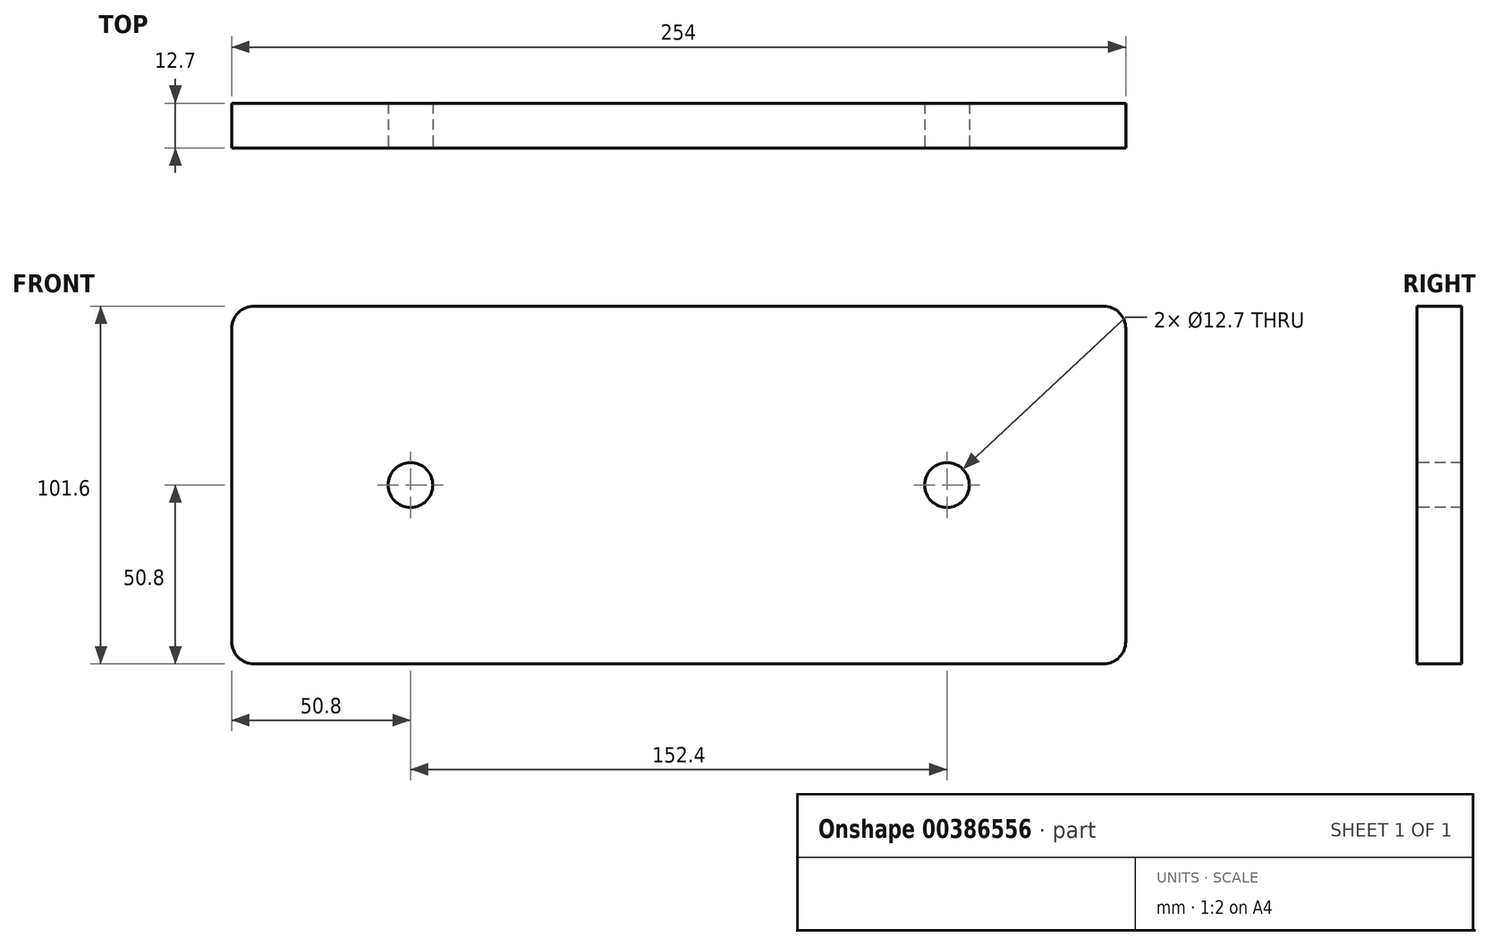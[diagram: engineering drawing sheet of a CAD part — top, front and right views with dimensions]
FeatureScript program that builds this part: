
annotation { "Feature Type Name" : "Feature", "Feature Type Description" : "" }
export const myFeature = defineFeature(function(context is Context, id is Id, definition is map)
    precondition{}
    {
        {
            var Q0;
            Q0=qCreatedBy(makeId("Front.planeOp"),FACE);
            var sketch = newSketch(context, id + "F0", { "sketchPlane" : qUnion([Q0])});
            skLineSegment(sketch, "E0.bottom", {"start": v(0, 0) * mm, "end": v(254, 0) * mm});
            skLineSegment(sketch, "E0.top", {"start": v(0, 101.6) * mm, "end": v(254, 101.6) * mm});
            skLineSegment(sketch, "E0.left", {"start": v(0, 0) * mm, "end": v(0, 101.6) * mm});
            skLineSegment(sketch, "E0.right", {"start": v(254, 0) * mm, "end": v(254, 101.6) * mm});
            skSolve(sketch);
        }
        {
            var Q0;
            Q0 = qSketchRegion(id + "F0", true);
            extrude(context, id + "F1", {"entities" : qUnion([Q0]), "depth" : 12.7 * mm});
        }
        {
            var Q0;
            Q0=makeQuery(id+"F1.opExtrude","CAP_FACE",FACE,{"disambiguationData":[OSD([sQuery(id+"F0.wireOp",EDGE,"E0.bottom"),sQuery(id+"F0.wireOp",EDGE,"E0.top"),sQuery(id+"F0.wireOp",EDGE,"E0.left"),sQuery(id+"F0.wireOp",EDGE,"E0.right")])],"isStart":false});
            var sketch = newSketch(context, id + "F2", { "sketchPlane" : qUnion([Q0])});
            skPoint(sketch, "E1", {"position": v(50.8, 50.8) * mm});
            skPoint(sketch, "E2", {"position": v(203.2, 50.8) * mm});
            skSolve(sketch);
        }
        {
            var Q0;
            Q0=sQuery(id+"F2.wireOp",VERTEX,"E1");
            var Q1;
            Q1=sQuery(id+"F2.wireOp",VERTEX,"E2");
            var Q2;
            Q2=makeQuery(id+"F1.opExtrude","SWEPT_BODY",BODY,{"disambiguationData":[OSD([sQuery(id+"F0.wireOp",EDGE,"E0.bottom"),sQuery(id+"F0.wireOp",EDGE,"E0.top"),sQuery(id+"F0.wireOp",EDGE,"E0.left"),sQuery(id+"F0.wireOp",EDGE,"E0.right")])]});
            hole(context, id + "F3", {"style" : HoleStyle.SIMPLE, "endStyle" : HoleEndStyle.THROUGH, "holeDiameter" : 12.7 * mm, "isTappedThrough" : true, "tappedDepth" : 12.7 * mm, "tapClearance" : 3, "startFromSketch" : true, "locations" : qUnion([Q0, Q1]), "scope" : qUnion([Q2])});
        }
        {
            var Q0;
            Q0=makeQuery(id+"F1.opExtrude","SWEPT_EDGE",EDGE,{"disambiguationData":[OSD([sQuery(id+"F0.wireOp",EDGE,"E0.top"),sQuery(id+"F0.wireOp",EDGE,"E0.left")])]});
            var Q1;
            Q1=makeQuery(id+"F1.opExtrude","SWEPT_EDGE",EDGE,{"disambiguationData":[OSD([sQuery(id+"F0.wireOp",EDGE,"E0.bottom"),sQuery(id+"F0.wireOp",EDGE,"E0.left")])]});
            var Q2;
            Q2=makeQuery(id+"F1.opExtrude","SWEPT_EDGE",EDGE,{"disambiguationData":[OSD([sQuery(id+"F0.wireOp",EDGE,"E0.bottom"),sQuery(id+"F0.wireOp",EDGE,"E0.right")])]});
            var Q3;
            Q3=makeQuery(id+"F1.opExtrude","SWEPT_EDGE",EDGE,{"disambiguationData":[OSD([sQuery(id+"F0.wireOp",EDGE,"E0.top"),sQuery(id+"F0.wireOp",EDGE,"E0.right")])]});
            fillet(context, id + "F4", {"entities" : qUnion([Q0, Q1, Q2, Q3]), "radius" : 6.35 * mm, "tangentPropagation" : true, "allowEdgeOverflow" : false});
        }
    });
